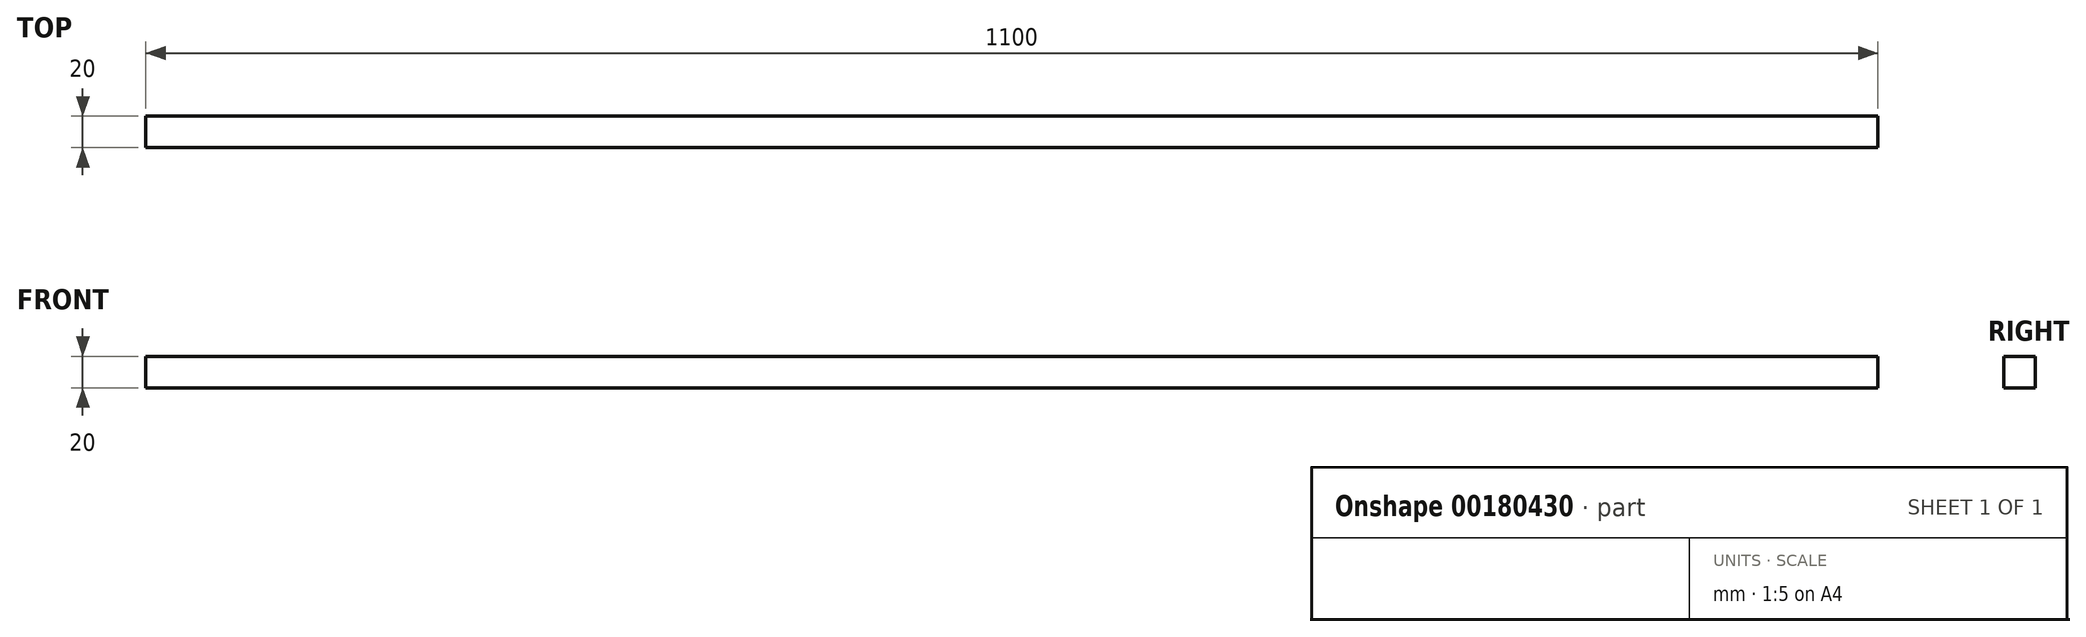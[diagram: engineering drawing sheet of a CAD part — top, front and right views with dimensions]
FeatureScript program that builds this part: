
annotation { "Feature Type Name" : "Feature", "Feature Type Description" : "" }
export const myFeature = defineFeature(function(context is Context, id is Id, definition is map)
    precondition{}
    {
        {
            var Q0;
            Q0=qCreatedBy(makeId("Top.planeOp"),FACE);
            var sketch = newSketch(context, id + "F0", { "sketchPlane" : qUnion([Q0])});
            skLineSegment(sketch, "E0.bottom", {"start": v(-520.54, -186.5) * mm, "end": v(579.46, -186.5) * mm});
            skLineSegment(sketch, "E0.top", {"start": v(-520.54, -166.5) * mm, "end": v(579.46, -166.5) * mm});
            skLineSegment(sketch, "E0.left", {"start": v(-520.54, -186.5) * mm, "end": v(-520.54, -166.5) * mm});
            skLineSegment(sketch, "E0.right", {"start": v(579.46, -186.5) * mm, "end": v(579.46, -166.5) * mm});
            skSolve(sketch);
        }
        {
            var Q0;
            Q0=makeQuery(id+"F0.imprint","IMPRINT",FACE,{"disambiguationData":[TD([[makeQuery(id+"F0.imprint","IMPRINT",EDGE,{"derivedFrom":sQuery(id+"F0.wireOp",EDGE,"E0.bottom")}),1.0]])]});
            extrude(context, id + "F1", {"entities" : qUnion([Q0]), "depth" : 20 * mm});
        }
    });
